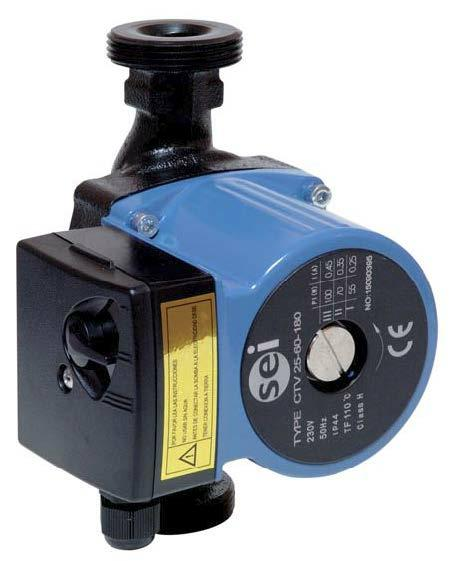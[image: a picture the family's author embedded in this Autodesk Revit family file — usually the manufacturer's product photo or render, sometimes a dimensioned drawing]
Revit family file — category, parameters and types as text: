
# Revit family: CTV_25-40-AC52120
name_source: partatom
category: Aparatos eléctricos
revit_build: Autodesk Revit 2016 (Build: 20150220_1215(x64)
units: mm (PartAtom-declared; Revit-internal decimal feet)

## family parameters
Compartido = No
Corte con vacíos al cargar = No
Cota de conector redondo = Diámetro de uso
Mantener orientación de anotación = No
Número OmniClass = 23.80.00.00
Punto de cálculo de habitación = No
Se basa en plano de trabajo = No
Siempre vertical = Sí
Tipo de pieza = Caja de conexiones
Título OmniClass = Electric Power and Lighting

## types (2) — shared parameters
Fabricante = SALVADOR ESCODA
URL = www.salvadorescoda.com
zero-valued in all types: Costo

## per-type parameters (varying)
| type | Aislamiento | Caudal | Conexión rácores | Código de montaje | Descripción | Dimensiones Unidad Interior | Imagen de tipo | Intensidad máx. | Modelo | Motor | Máx. presión trabajo | Peso | Potencia máx | Presión disponible | Protección | Rango temperatura agua | Regulable | Temperatura ambiente |
| MVD-22T2 | 35 dB(A) |  |  | CL23370 | CONDUCTO BAJA SILUETA | 700 x 210 x 500 mm | <Ninguno> |  | MVD-22T2/DHN1-DA5 | 521 m3/h | 2,2kW / 39W | 17,5 kg neto |  |  | 6,35 mm (1/4") | 2,6kW / 39W |  | DC / WZDK100-38GS |
| CTV | Clase H | 1,5 m3/h | 1 1/2" DN | AC52120 | BOMBA CIRCULADORA PARA CALEFACCION | 180 x 130 x 130 mm | SEI_CTV.jpg | 0,28 A | CTV 25-40 | 2 polos, 1x230V - 50Hz | 10 bar | 3,15 Kgs | 65 W | 2,5 m.c.a. | IP 44 | 2º a 110 ºC | 3 velocidades | Hasta 40ºC |
